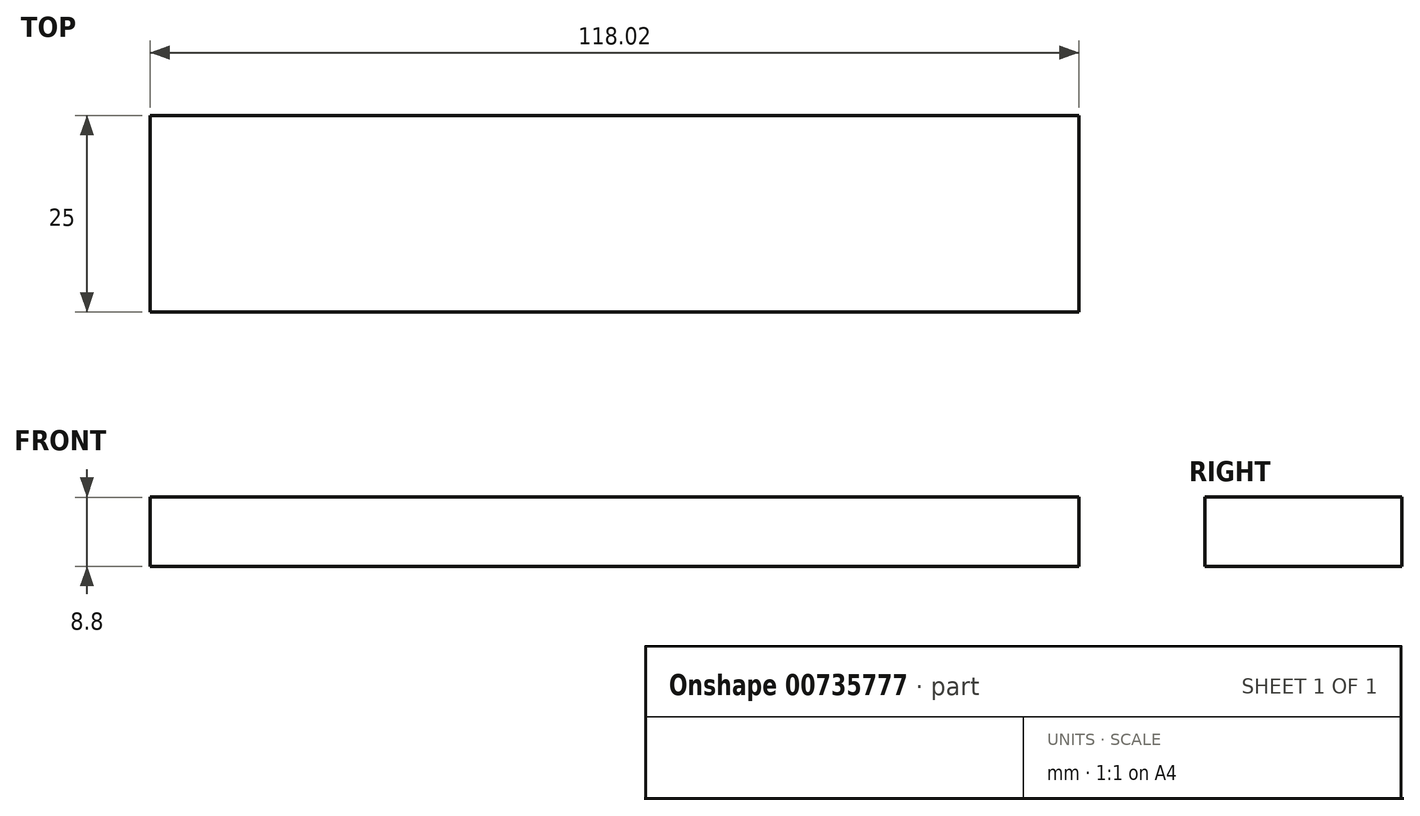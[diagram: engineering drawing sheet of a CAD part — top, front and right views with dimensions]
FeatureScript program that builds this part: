
annotation { "Feature Type Name" : "Feature", "Feature Type Description" : "" }
export const myFeature = defineFeature(function(context is Context, id is Id, definition is map)
    precondition{}
    {
        {
            var Q0;
            Q0=qCreatedBy(makeId("Front.planeOp"),FACE);
            var sketch = newSketch(context, id + "F0", { "sketchPlane" : qUnion([Q0])});
            skLineSegment(sketch, "E0.bottom", {"start": v(-59, 4.4) * mm, "end": v(59, 4.4) * mm});
            skLineSegment(sketch, "E0.top", {"start": v(-59, -4.4) * mm, "end": v(59, -4.4) * mm});
            skLineSegment(sketch, "E0.left", {"start": v(-59, 4.4) * mm, "end": v(-59, -4.4) * mm});
            skLineSegment(sketch, "E0.right", {"start": v(59, 4.4) * mm, "end": v(59, -4.4) * mm});
            skPoint(sketch, "E0.middle", {"position": v(0, 0) * mm});
            skSolve(sketch);
        }
        {
            var Q0;
            Q0 = qSketchRegion(id + "F0", true);
            extrude(context, id + "F1", {"entities" : qUnion([Q0]), "depth" : 25 * mm, "offsetDistance" : 25 * mm});
        }
    });
